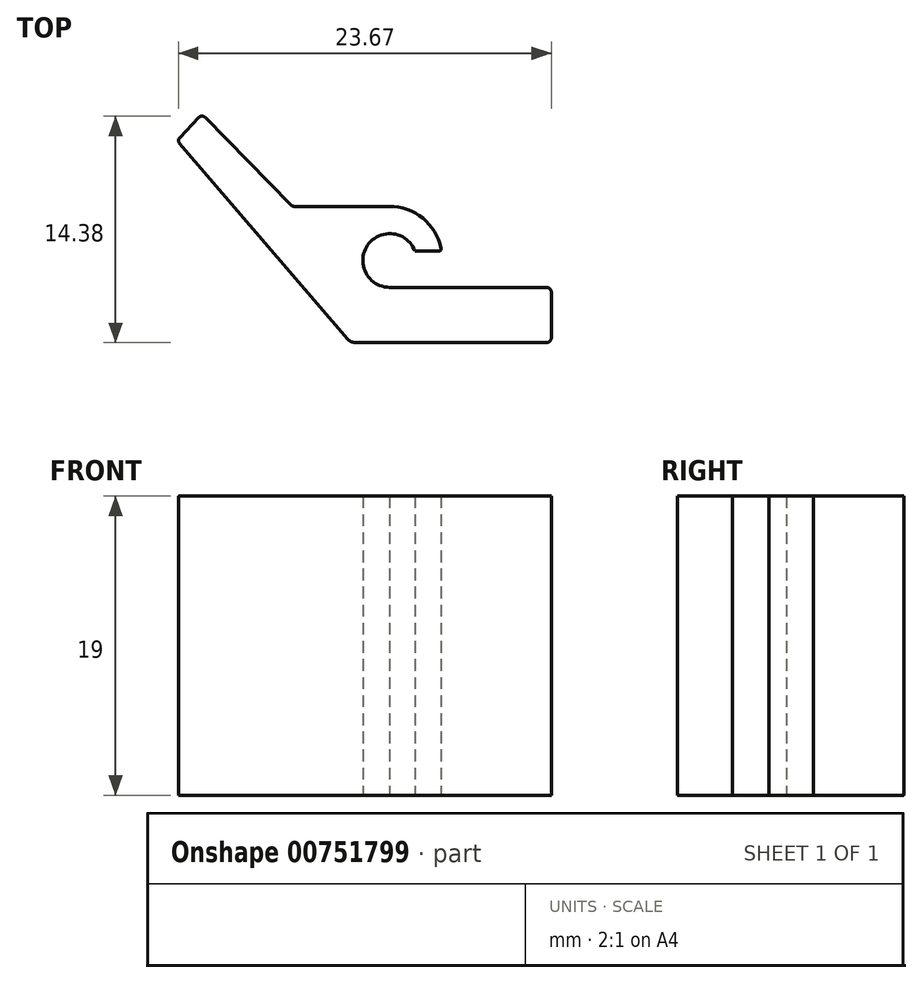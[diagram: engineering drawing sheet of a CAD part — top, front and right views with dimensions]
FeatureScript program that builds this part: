
annotation { "Feature Type Name" : "Feature", "Feature Type Description" : "" }
export const myFeature = defineFeature(function(context is Context, id is Id, definition is map)
    precondition{}
    {
        {
            var Q0;
            Q0=qCreatedBy(makeId("Top.planeOp"),FACE);
            var sketch = newSketch(context, id + "F0", { "sketchPlane" : qUnion([Q0])});
            skLineSegment(sketch, "E0", {"start": v(0.32, 0) * mm, "end": v(12.44, 0) * mm});
            skCircle(sketch, "E1", {"center": v(0, 0) * mm, "radius": 16.93 * mm, "construction": true});
            skCircle(sketch, "E2", {"center": v(12.74, 0) * mm, "radius": 27.02 * mm, "construction": true});
            skLineSegment(sketch, "E3", {"start": v(-0.2, 0.24) * mm, "end": v(-10.86, 12.63) * mm});
            skLineSegment(sketch, "E4", {"start": v(12.74, 0.3) * mm, "end": v(12.74, 3.2) * mm});
            skLineSegment(sketch, "E5", {"start": v(12.44, 3.51) * mm, "end": v(-3.02, 3.51) * mm});
            skLineSegment(sketch, "E6", {"start": v(-10.85, 13.04) * mm, "end": v(-9.66, 14.3) * mm});
            skCircle(sketch, "E7", {"center": v(-3.02, 3.51) * mm, "radius": 4.55 * mm, "construction": true});
            skLineSegment(sketch, "E8", {"start": v(-9.23, 14.3) * mm, "end": v(-3.82, 8.77) * mm});
            skLineSegment(sketch, "E9", {"start": v(1.53, 3.51) * mm, "end": v(1.53, 6.95) * mm, "construction": true});
            skCircle(sketch, "E10", {"center": v(12.74, 3.5) * mm, "radius": 12 * mm, "construction": true});
            skLineSegment(sketch, "E11", {"start": v(0.74, 3.51) * mm, "end": v(0.74, 5.23) * mm, "construction": true});
            skLineSegment(sketch, "E12", {"start": v(0.86, 5.23) * mm, "end": v(0.74, 5.23) * mm, "construction": true});
            skPoint(sketch, "E13.orphan", {"position": v(1.53, 5.23) * mm});
            skLineSegment(sketch, "E14", {"start": v(0.74, 5.23) * mm, "end": v(4.18, 5.23) * mm, "construction": true});
            skCircle(sketch, "E15", {"center": v(2.46, 5.23) * mm, "radius": 1.72 * mm, "construction": true});
            skLineSegment(sketch, "E16", {"start": v(2.46, 6.95) * mm, "end": v(2.46, 8.65) * mm, "construction": true});
            skLineSegment(sketch, "E17", {"start": v(2.46, 8.65) * mm, "end": v(-3.54, 8.65) * mm});
            skLineSegment(sketch, "E18", {"start": v(12.74, 3.5) * mm, "end": v(12.74, 5.81) * mm, "construction": true});
            skLineSegment(sketch, "E19", {"start": v(5.61, 5.81) * mm, "end": v(4.08, 5.81) * mm, "construction": true});
            skArc(sketch, "E20", {"start": v(4.08, 5.81) * mm, "mid": v(1.08, 6.2) * mm, "end": v(2.46, 3.5) * mm});
            skLineSegment(sketch, "E21", {"start": v(4.08, 5.81) * mm, "end": v(5.61, 5.81) * mm});
            skArc(sketch, "E22", {"start": v(5.75, 5.98) * mm, "mid": v(4.58, 7.9) * mm, "end": v(2.46, 8.65) * mm});
            skArc(sketch, "E23.filletArc", {"start": v(5.61, 5.81) * mm, "mid": v(5.72, 5.86) * mm, "end": v(5.75, 5.98) * mm});
            skArc(sketch, "E24.filletArc", {"start": v(-3.82, 8.77) * mm, "mid": v(-3.7, 8.68) * mm, "end": v(-3.54, 8.65) * mm});
            skPoint(sketch, "E25.visualSharp", {"position": v(-9.45, 14.52) * mm});
            skArc(sketch, "E25.filletArc", {"start": v(-9.23, 14.3) * mm, "mid": v(-9.44, 14.38) * mm, "end": v(-9.66, 14.3) * mm});
            skPoint(sketch, "E26.visualSharp", {"position": v(-11.03, 12.84) * mm});
            skArc(sketch, "E26.filletArc", {"start": v(-10.85, 13.04) * mm, "mid": v(-10.93, 12.84) * mm, "end": v(-10.86, 12.63) * mm});
            skArc(sketch, "E27.filletArc", {"start": v(-0.2, 0.24) * mm, "mid": v(0.03, 0.06) * mm, "end": v(0.32, 0) * mm});
            skArc(sketch, "E28.filletArc", {"start": v(12.44, 0) * mm, "mid": v(12.65, 0.09) * mm, "end": v(12.74, 0.3) * mm});
            skArc(sketch, "E29.filletArc", {"start": v(12.74, 3.2) * mm, "mid": v(12.65, 3.42) * mm, "end": v(12.44, 3.5) * mm});
            skSolve(sketch);
        }
        {
            var Q0;
            Q0=makeQuery(id+"F0.imprint","IMPRINT",FACE,{"disambiguationData":[TD([[makeQuery(id+"F0.imprint","IMPRINT",EDGE,{"derivedFrom":sQuery(id+"F0.wireOp",EDGE,"E6")}),-1.0]])]});
            var Q1;
            Q1=makeQuery(id+"F0.imprint","IMPRINT",FACE,{"disambiguationData":[TD([[makeQuery(id+"F0.imprint","IMPRINT",EDGE,{"derivedFrom":sQuery(id+"F0.wireOp",EDGE,"E0")}),1.0]])]});
            extrude(context, id + "F1", {"entities" : qUnion([Q0, Q1]), "depth" : 19 * mm, "offsetDistance" : 25 * mm});
        }
    });
